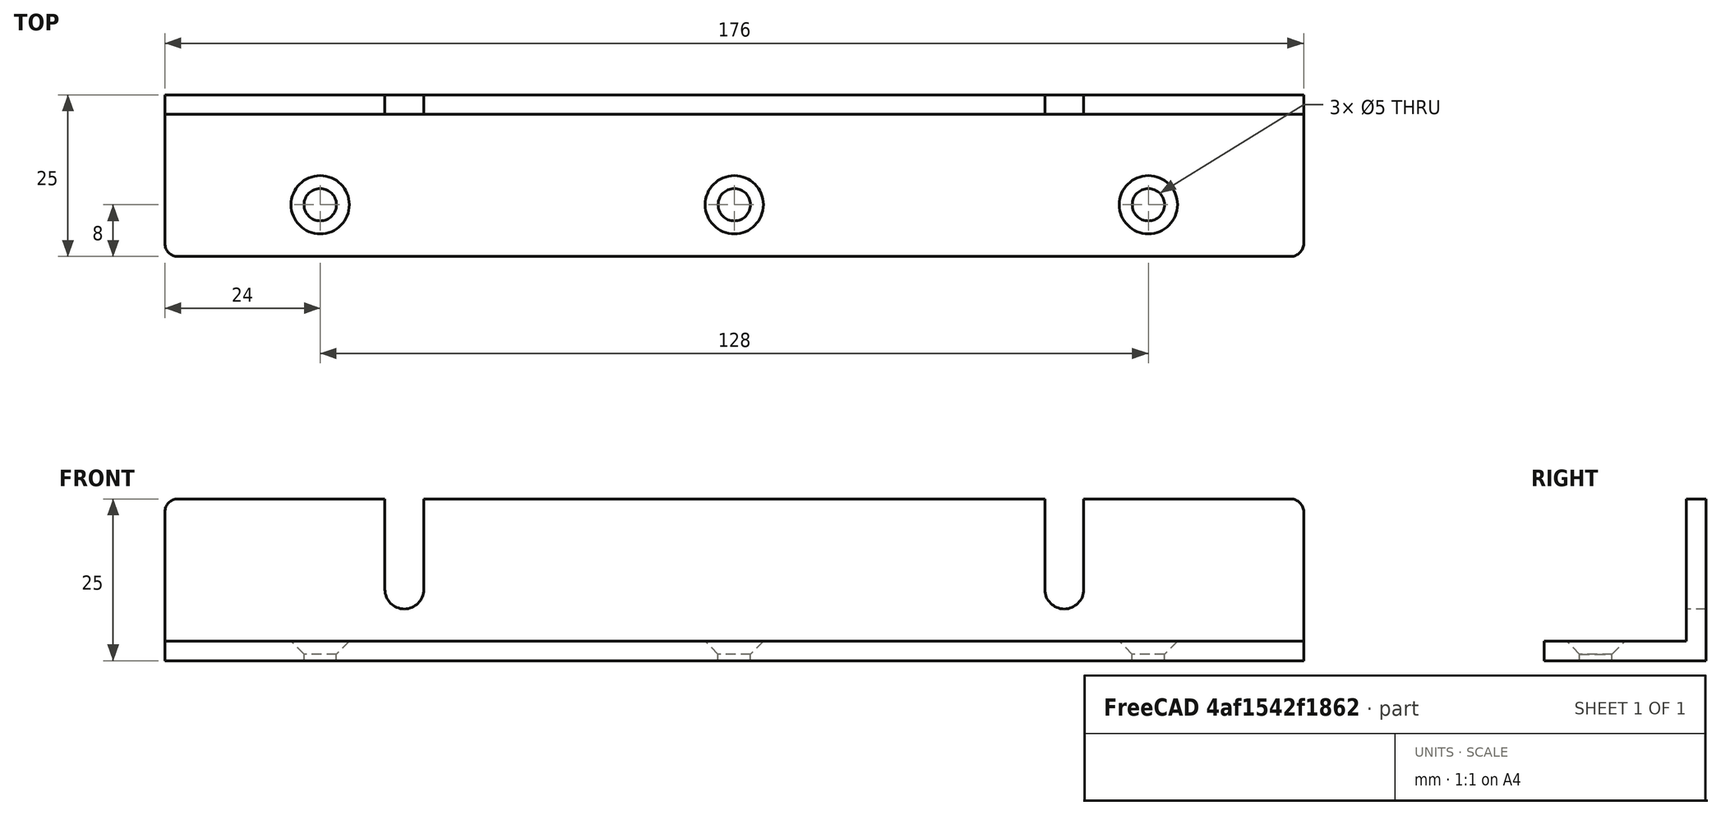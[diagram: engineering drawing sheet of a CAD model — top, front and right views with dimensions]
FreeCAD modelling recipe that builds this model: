
FCSTD DOCUMENT  (FreeCAD 0.15R4671 (Git))
Label: rack-ears
License: All rights reserved
LicenseURL: http://en.wikipedia.org/wiki/All_rights_reserved
objects: Drawing::FeatureView×7, Part::Cylinder×5, Part::Cut×5, Part::Box×4, Part::Fuse×2, Part::Fillet×2, Drawing::FeatureViewPart×2, Part::Chamfer×1, Part::MultiFuse×1, Drawing::FeaturePage×1
note: 20 computed .brp shape members not serialized (recipe doc carries the construction recipe); baked Part::Feature solids carry a one-line shape summary decoded from their .brp

FEATURE [Part::Box] Box  label="Cube"
  Height = 3
  Length = 176
  Placement = pos=(0,1,0) rot=(0,0,1;0rad)
  Width = 25
FEATURE [Part::Cylinder] Cylinder
  Angle = 360
  Height = 10
  Placement = pos=(24,9,0) rot=(0,0,1;0rad)
  Radius = 2.5
FEATURE [Part::Cylinder] Cylinder001
  Angle = 360
  Height = 10
  Placement = pos=(152,9,0) rot=(0,0,1;0rad)
  Radius = 2.5
FEATURE [Part::Cylinder] Cylinder002
  Angle = 360
  Height = 10
  Placement = pos=(88,9,0) rot=(0,0,1;0rad)
  Radius = 2.5
FEATURE [Part::Cut] Cut
  Base = -> Box
  Tool = -> Cylinder
FEATURE [Part::Cut] Cut001
  Base = -> Cut
  Tool = -> Cylinder001
FEATURE [Part::Cut] Cut002
  Base = -> Cut001
  Tool = -> Cylinder002
FEATURE [Part::Chamfer] Chamfer
  Base = -> Cut002
  Edges = 3 edges r=2: [Edge10,Edge11,Edge12]
FEATURE [Part::Box] Box001  label="Cube001"
  Height = 3
  Length = 176
  Placement = pos=(0,26,0) rot=(1,0,0;1.5708rad)
  Width = 25
FEATURE [Part::Box] Box002  label="Cube002"
  Height = 15
  Length = 6
  Placement = pos=(33,0,0) rot=(0,0,1;0rad)
  Width = 6
FEATURE [Part::Cylinder] Cylinder003
  Angle = 360
  Height = 6
  Placement = pos=(36,6,0) rot=(1,0,0;1.5708rad)
  Radius = 3
FEATURE [Part::Fuse] Fusion
  Base = -> Box002
  Placement = pos=(1,22,11) rot=(0,0,1;0rad)
  Tool = -> Cylinder003
FEATURE [Part::Box] Box003  label="Cube003"
  Height = 15
  Length = 6
  Placement = pos=(33,0,0) rot=(0,0,1;0rad)
  Width = 6
FEATURE [Part::Cylinder] Cylinder004
  Angle = 360
  Height = 6
  Placement = pos=(36,6,0) rot=(1,0,0;1.5708rad)
  Radius = 3
FEATURE [Part::Fuse] Fusion001
  Base = -> Box003
  Placement = pos=(103,22,11) rot=(0,0,1;0rad)
  Tool = -> Cylinder004
FEATURE [Part::Cut] Cut003
  Base = -> Box001
  Tool = -> Fusion
FEATURE [Part::Cut] Cut004
  Base = -> Cut003
  Tool = -> Fusion001
FEATURE [Part::Fillet] Fillet
  Base = -> Chamfer
  Edges = 2 edges r=2: [Edge10,Edge16]
FEATURE [Part::Fillet] Fillet001
  Base = -> Cut004
  Edges = 2 edges r=2: [Edge3,Edge29]
FEATURE [Part::MultiFuse] Fusion002  label="4U Ears"
  Shapes = -> [Fillet001,Fillet]
FEATURE [Drawing::FeatureViewPart] Ortho006  label="Ortho_1_0"
  Direction = (0,1,0)
  HiddenWidth = 0.15
  LineWidth = 0.35
  Rotation = -90
  ShowHiddenLines = false
  ShowSmoothLines = false
  Source = -> Fusion002
  Tolerance = 0.05
  ViewResult = <g id="Ortho_1_0"\n   transform="rotate(-90,250,130) translate(250,130) scale(1,1)"\n  >\n<g   stroke="rgb(0, 0, 0)"\n   stroke-width="0.35"\n   stroke-linecap="butt"\n   stroke-linejoin="miter"\n   fill="none"\n   transform="scale(1,-1)"\n  >\n<path d="M23 -4.44089e-016 A2 2 0 0 1 25 2" /><path id= "2" d=" M 25 2 L 25 34 " />\n<path id= "3" d=" M 11 34 L 25 34 " />\n<path d="M11 34 A3 3 0 0 0 11 40" /><path id= "5" d=" M 11 40 L 25 40 " />\n<path id= "6" d=" M 25 40 L 25 136 " />\n<path id= "7" d=" M 11 136 L 25 136 " />\n<path d="M11 136 A3 3 0 1 0 11 142" /><path id= "9" d=" M 11 142 L 25 142 " />\n<path id= "10" d=" M 25 142 L 25 174 " />\n<path d="M23 176 A2 2 0 0 0 25 174" /><path id= "12" d=" M 3 176 L 23 176 " />\n<path id= "13" d=" M 3 0 L 3 176 " />\n<path id= "14" d=" M 3 0 L 23 0 " />\n<path id= "15" d=" M 0 176 L 3 176 " />\n<path id= "16" d=" M 0 0 L 0 176 " />\n<path id= "17" d=" M 0 0 L 3 0 " />\n<path id= "18" d=" M 0 -4.44089e-016 L 3 -4.44089e-016 " />\n<path id= "19" d=" M 0 176 L 3 176 " />\n</g>\n</g>
  Visible = true
  X = 250
  Y = 130
FEATURE [Drawing::FeatureViewPart] Ortho007  label="Ortho_0_1"
  Direction = (0,0,1)
  HiddenWidth = 0.15
  LineWidth = 0.35
  Rotation = 180
  ShowHiddenLines = false
  ShowSmoothLines = false
  Source = -> Fusion002
  Tolerance = 0.05
  ViewResult = <blob: 2839 chars omitted>
  Visible = true
  X = 250
  Y = 50
FEATURE [Drawing::FeatureView] centerLines
  Rotation = 0
  ViewResult = <g transform="scale(1.000000,1.000000)" stroke="rgb(0,0,0)"  stroke-width="0.300000" > <path d="M 162.000000,59.000000 L 162.000000,61.000000 M 162.000000,63.000000 L 162.000000,69.000000 M 162.000000,71.000000 L 162.000000,73.000000 M 162.000000,75.000000 L 162.000000,81.000000 M 162.000000,83.000000 L 162.000000,85.000000 M 162.000000,87.000000 L 162.000000,93.000000 M 162.000000,95.000000 L 162.000000,97.000000 M 162.000000,99.000000 L 162.000000,105.000000 M 162.000000,107.000000 L 162.000000,109.000000 M 162.000000,111.000000 L 162.000000,117.000000 M 162.000000,119.000000 L 162.000000,121.000000 M 162.000000,123.000000 L 162.000000,129.000000 M 162.000000,131.000000 L 162.000000,133.000000 M 162.000000,135.000000 L 162.000000,141.000000 "/>\n<path d="M 162.000000,59.000000 L 162.000000,57.000000 M 162.000000,55.000000 L 162.000000,49.000000 M 162.000000,47.000000 L 162.000000,45.000000 M 162.000000,43.000000 L 162.000000,37.000000 M 162.000000,35.000000 L 162.000000,33.000000 M 162.000000,31.000000 L 162.000000,25.000000 "/> </g> 
  Visible = true
  X = 0
  Y = 0
FEATURE [Drawing::FeatureView] dim001
  Rotation = 0
  ViewResult = <g> \n  <line x1="226.000000" y1="52.500000" x2="226.000000" y2="33.891969" style="stroke:rgb(0,0,0);stroke-width:0.30" />\n<line x1="250.000000" y1="51.000000" x2="250.000000" y2="33.891969" style="stroke:rgb(0,0,0);stroke-width:0.30" />\n<line x1="226.000000" y1="34.891969" x2="250.000000" y2="34.891969" style="stroke:rgb(0,0,0);stroke-width:0.30" /> \n  <polygon points="250.000000,34.891969 247.000000,33.891969 246.000000,34.891969 247.000000,35.891969" style="fill:rgb(0,0,0);stroke:rgb(0,0,0);stroke-width:0" /><polygon points="226.000000,34.891969 229.000000,35.891969 230.000000,34.891969 229.000000,33.891969" style="fill:rgb(0,0,0);stroke:rgb(0,0,0);stroke-width:0" /> \n  <text x="238.000000" y="32.891969" font-family="arial" font-size="3.6" fill="rgb(0,0,0)" text-anchor="middle" transform="rotate(0.000000 238.000000,32.891969)" >24</text> </g>
  Visible = true
  X = 0
  Y = 0
FEATURE [Drawing::FeatureView] dim004
  Rotation = 0
  ViewResult = <g> \n  <line x1="162.000000" y1="65.500000" x2="162.000000" y2="84.978550" style="stroke:rgb(0,0,0);stroke-width:0.30" />\n<line x1="74.000000" y1="78.000000" x2="74.000000" y2="84.978550" style="stroke:rgb(0,0,0);stroke-width:0.30" />\n<line x1="162.000000" y1="83.978550" x2="74.000000" y2="83.978550" style="stroke:rgb(0,0,0);stroke-width:0.30" /> \n  <polygon points="74.000000,83.978550 77.000000,84.978550 78.000000,83.978550 77.000000,82.978550" style="fill:rgb(0,0,0);stroke:rgb(0,0,0);stroke-width:0" /><polygon points="162.000000,83.978550 159.000000,82.978550 158.000000,83.978550 159.000000,84.978550" style="fill:rgb(0,0,0);stroke:rgb(0,0,0);stroke-width:0" /> \n  <text x="118.000000" y="81.978550" font-family="arial" font-size="3.6" fill="rgb(0,0,0)" text-anchor="middle" transform="rotate(0.000000 118.000000,81.978550)" >88</text> </g>
  Visible = true
  X = 0
  Y = 0
FEATURE [Drawing::FeatureView] dim005
  Rotation = 0
  ViewResult = <g> \n  <line x1="74.000000" y1="132.000000" x2="74.000000" y2="151.815878" style="stroke:rgb(0,0,0);stroke-width:0.30" />\n<line x1="250.000000" y1="132.000000" x2="250.000000" y2="151.815878" style="stroke:rgb(0,0,0);stroke-width:0.30" />\n<line x1="74.000000" y1="150.815878" x2="250.000000" y2="150.815878" style="stroke:rgb(0,0,0);stroke-width:0.30" /> \n  <polygon points="250.000000,150.815878 247.000000,149.815878 246.000000,150.815878 247.000000,151.815878" style="fill:rgb(0,0,0);stroke:rgb(0,0,0);stroke-width:0" /><polygon points="74.000000,150.815878 77.000000,151.815878 78.000000,150.815878 77.000000,149.815878" style="fill:rgb(0,0,0);stroke:rgb(0,0,0);stroke-width:0" /> \n  <text x="162.000000" y="148.815878" font-family="arial" font-size="3.6" fill="rgb(0,0,0)" text-anchor="middle" transform="rotate(0.000000 162.000000,148.815878)" >176</text> </g>
  Visible = true
  X = 0
  Y = 0
FEATURE [Drawing::FeatureView] dim006
  Rotation = 0
  ViewResult = <g> \n  <line x1="98.000000" y1="52.500000" x2="98.000000" y2="32.903340" style="stroke:rgb(0,0,0);stroke-width:0.30" />\n<line x1="74.000000" y1="51.000000" x2="74.000000" y2="32.903340" style="stroke:rgb(0,0,0);stroke-width:0.30" />\n<line x1="98.000000" y1="33.903340" x2="74.000000" y2="33.903340" style="stroke:rgb(0,0,0);stroke-width:0.30" /> \n  <polygon points="74.000000,33.903340 77.000000,34.903340 78.000000,33.903340 77.000000,32.903340" style="fill:rgb(0,0,0);stroke:rgb(0,0,0);stroke-width:0" /><polygon points="98.000000,33.903340 95.000000,32.903340 94.000000,33.903340 95.000000,34.903340" style="fill:rgb(0,0,0);stroke:rgb(0,0,0);stroke-width:0" /> \n  <text x="86.000000" y="31.903340" font-family="arial" font-size="3.6" fill="rgb(0,0,0)" text-anchor="middle" transform="rotate(0.000000 86.000000,31.903340)" >24</text> </g>
  Visible = true
  X = 0
  Y = 0
FEATURE [Drawing::FeatureView] dim008
  Rotation = 0
  ViewResult = <g> \n  <line x1="74.000000" y1="105.000000" x2="74.000000" y2="94.879510" style="stroke:rgb(0,0,0);stroke-width:0.30" />\n<line x1="108.000000" y1="103.000000" x2="108.000000" y2="94.879510" style="stroke:rgb(0,0,0);stroke-width:0.30" />\n<line x1="74.000000" y1="95.879510" x2="108.000000" y2="95.879510" style="stroke:rgb(0,0,0);stroke-width:0.30" /> \n  <polygon points="108.000000,95.879510 105.000000,94.879510 104.000000,95.879510 105.000000,96.879510" style="fill:rgb(0,0,0);stroke:rgb(0,0,0);stroke-width:0" /><polygon points="74.000000,95.879510 77.000000,96.879510 78.000000,95.879510 77.000000,94.879510" style="fill:rgb(0,0,0);stroke:rgb(0,0,0);stroke-width:0" /> \n  <text x="91.000000" y="93.879510" font-family="arial" font-size="3.6" fill="rgb(0,0,0)" text-anchor="middle" transform="rotate(0.000000 91.000000,93.879510)" >34</text> </g>
  Visible = true
  X = 0
  Y = 0
FEATURE [Drawing::FeatureView] dim009
  Rotation = 0
  ViewResult = <g> \n  <line x1="216.000000" y1="103.000000" x2="216.000000" y2="94.879510" style="stroke:rgb(0,0,0);stroke-width:0.30" />\n<line x1="250.000000" y1="105.000000" x2="250.000000" y2="94.879510" style="stroke:rgb(0,0,0);stroke-width:0.30" />\n<line x1="216.000000" y1="95.879510" x2="250.000000" y2="95.879510" style="stroke:rgb(0,0,0);stroke-width:0.30" /> \n  <polygon points="250.000000,95.879510 247.000000,94.879510 246.000000,95.879510 247.000000,96.879510" style="fill:rgb(0,0,0);stroke:rgb(0,0,0);stroke-width:0" /><polygon points="216.000000,95.879510 219.000000,96.879510 220.000000,95.879510 219.000000,94.879510" style="fill:rgb(0,0,0);stroke:rgb(0,0,0);stroke-width:0" /> \n  <text x="233.000000" y="93.879510" font-family="arial" font-size="3.6" fill="rgb(0,0,0)" text-anchor="middle" transform="rotate(0.000000 233.000000,93.879510)" >34</text> </g>
  Visible = true
  X = 0
  Y = 0
FEATURE [Drawing::FeaturePage] Page
  EditableTexts = FLOYD DIEBEL | EMRL | 4U Rack Ears | 0001 | 2016-01-28
  Group = -> [Ortho006,Ortho007,centerLines,dim001,dim004,dim005,dim006,dim008,dim009]
  Template = D:/Program Files/FreeCAD 0.15/data/Mod/Drawing/Templates/A4_Landscape_ISO7200.svg
